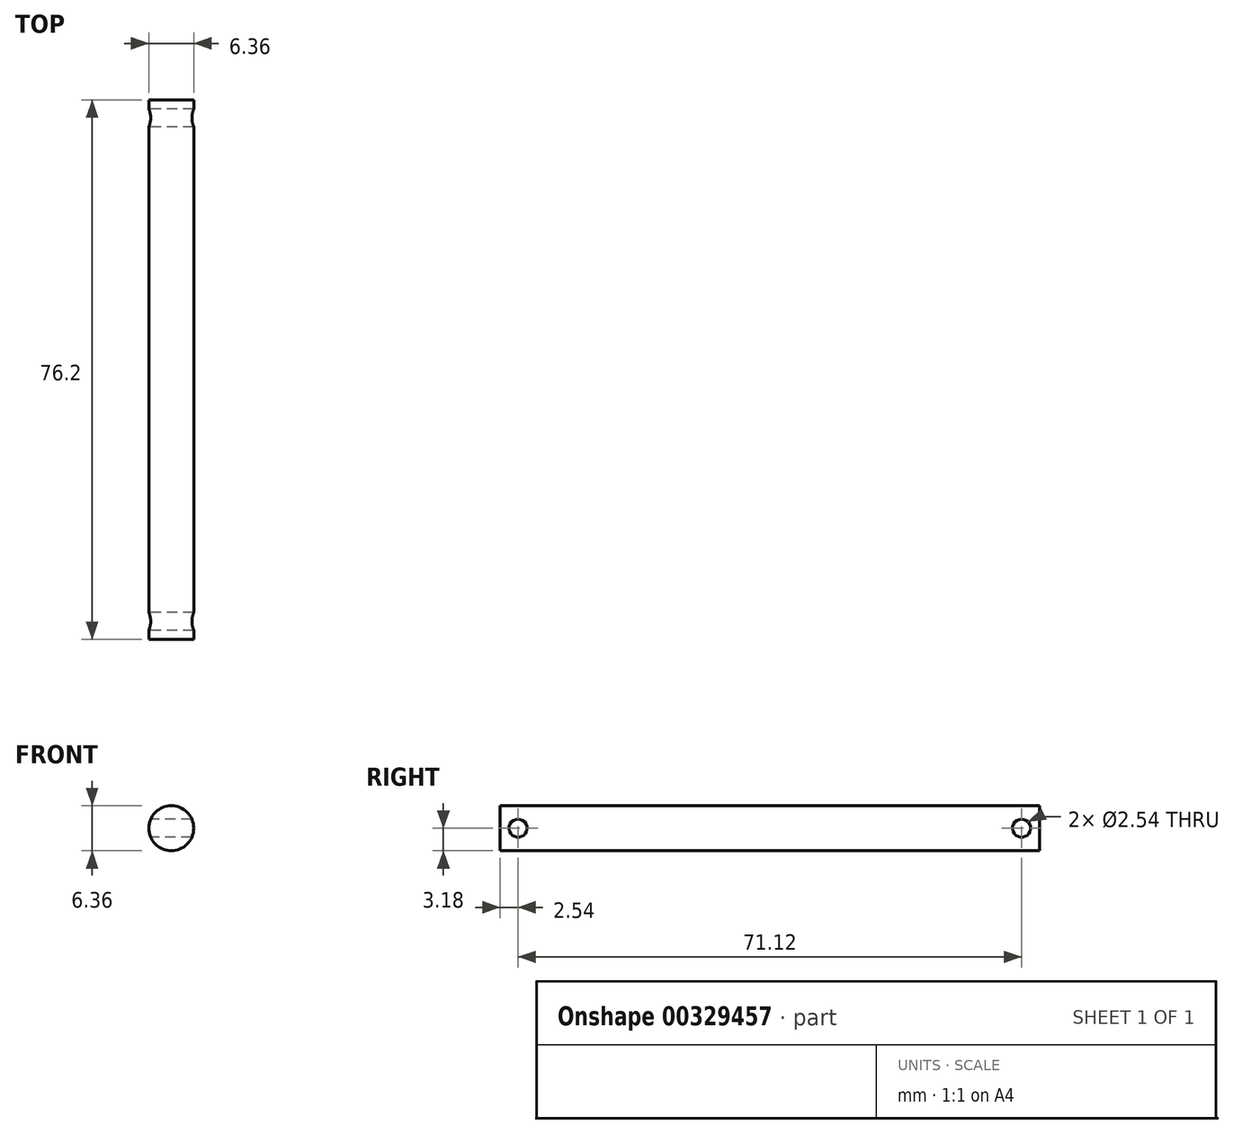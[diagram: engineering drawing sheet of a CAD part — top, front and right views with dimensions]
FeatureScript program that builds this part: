
annotation { "Feature Type Name" : "Feature", "Feature Type Description" : "" }
export const myFeature = defineFeature(function(context is Context, id is Id, definition is map)
    precondition{}
    {
        {
            var Q0;
            Q0=qCreatedBy(makeId("Front.planeOp"),FACE);
            var sketch = newSketch(context, id + "F0", { "sketchPlane" : qUnion([Q0])});
            skCircle(sketch, "E0", {"center": v(0, 0) * mm, "radius": 3.18 * mm});
            skSolve(sketch);
        }
        {
            var Q0;
            Q0 = qSketchRegion(id + "F0", true);
            extrude(context, id + "F1", {"entities" : qUnion([Q0]), "oppositeDirection" : true, "depth" : 76.2 * mm});
        }
        {
            var Q0;
            Q0=qCreatedBy(makeId("Right.planeOp"),FACE);
            var sketch = newSketch(context, id + "F2", { "sketchPlane" : qUnion([Q0])});
            skCircle(sketch, "E1", {"center": v(2.54, 0) * mm, "radius": 1.27 * mm});
            skCircle(sketch, "E2", {"center": v(73.66, 0) * mm, "radius": 1.27 * mm});
            skSolve(sketch);
        }
        {
            var Q0;
            Q0 = qSketchRegion(id + "F2", true);
            extrude(context, id + "F3", {"entities" : qUnion([Q0]), "operationType" : NewBodyOperationType.REMOVE, "endBound" : BoundingType.THROUGH_ALL, "depth" : 18.03 * mm});
        }
        {
            var Q0;
            Q0 = qSketchRegion(id + "F2", true);
            extrude(context, id + "F4", {"entities" : qUnion([Q0]), "operationType" : NewBodyOperationType.REMOVE, "endBound" : BoundingType.THROUGH_ALL, "oppositeDirection" : true, "depth" : 25.4 * mm});
        }
    });
